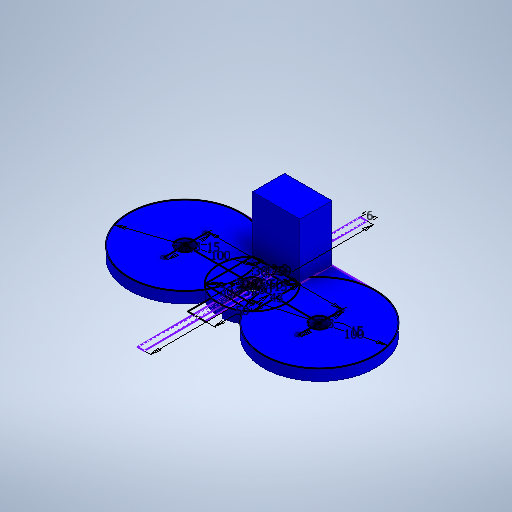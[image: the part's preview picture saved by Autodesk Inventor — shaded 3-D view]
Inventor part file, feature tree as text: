
AUTODESK INVENTOR PART (.ipt)
format: ipt  version: 2025.2 (Build 292293000, 293)  size: 309,760 bytes
history: native  units: mm
features: extrude x3, hole x2, sketch x1
ambient origin geometry x8: Origin, YZ Plane, XZ Plane, XY Plane, X Axis, Y Axis, Z Axis, Center Point
bodies: Body1 (feature_tree)
feature tree (6):
  sketch  "Sketch6"  dims[d37=120.0mm d38=60.0mm d39=100.0mm d40=100.0mm d41=15.0mm d42=15.0mm d43=15.0mm d44=10.0mm d45=0.0mm d46=37.3mm d47=37.3mm d48=30.759mm d49=30.759mm d50=30.759mm d51=3.5mm d52=6.0mm d53=4.0mm d54=2.0mm d55=90.0deg d56=8.0mm d57=20.594885mm d58=5.0mm d59=6.0mm d60=4.0mm d61=2.0mm d62=90.0deg d63=8.0mm d64=20.594885mm d65=42.3mm d66=43.0mm d67=50.0mm d70=6.0mm d71=200.0mm d72=15.0mm d73=0.0mm d74=50.0mm d75=0.0mm d5=0.5mm d6=0.872665mm d7=0.5mm d8=0.872665mm]
  extrude  "Extrusion8"  Depth=60.0mm
  hole  "Hole1"  [1 undecoded]
  hole  "Hole2"  [1 undecoded]
  extrude  "Extrusion10"  Depth=50.0mm
  extrude  "Extrusion11"  Depth=50.0mm
note: 2 required parameter values undecoded (feature->parameter linkage not recoverable at this tier; creation-order binding heuristic only, values carry confidence <= 0.55)
